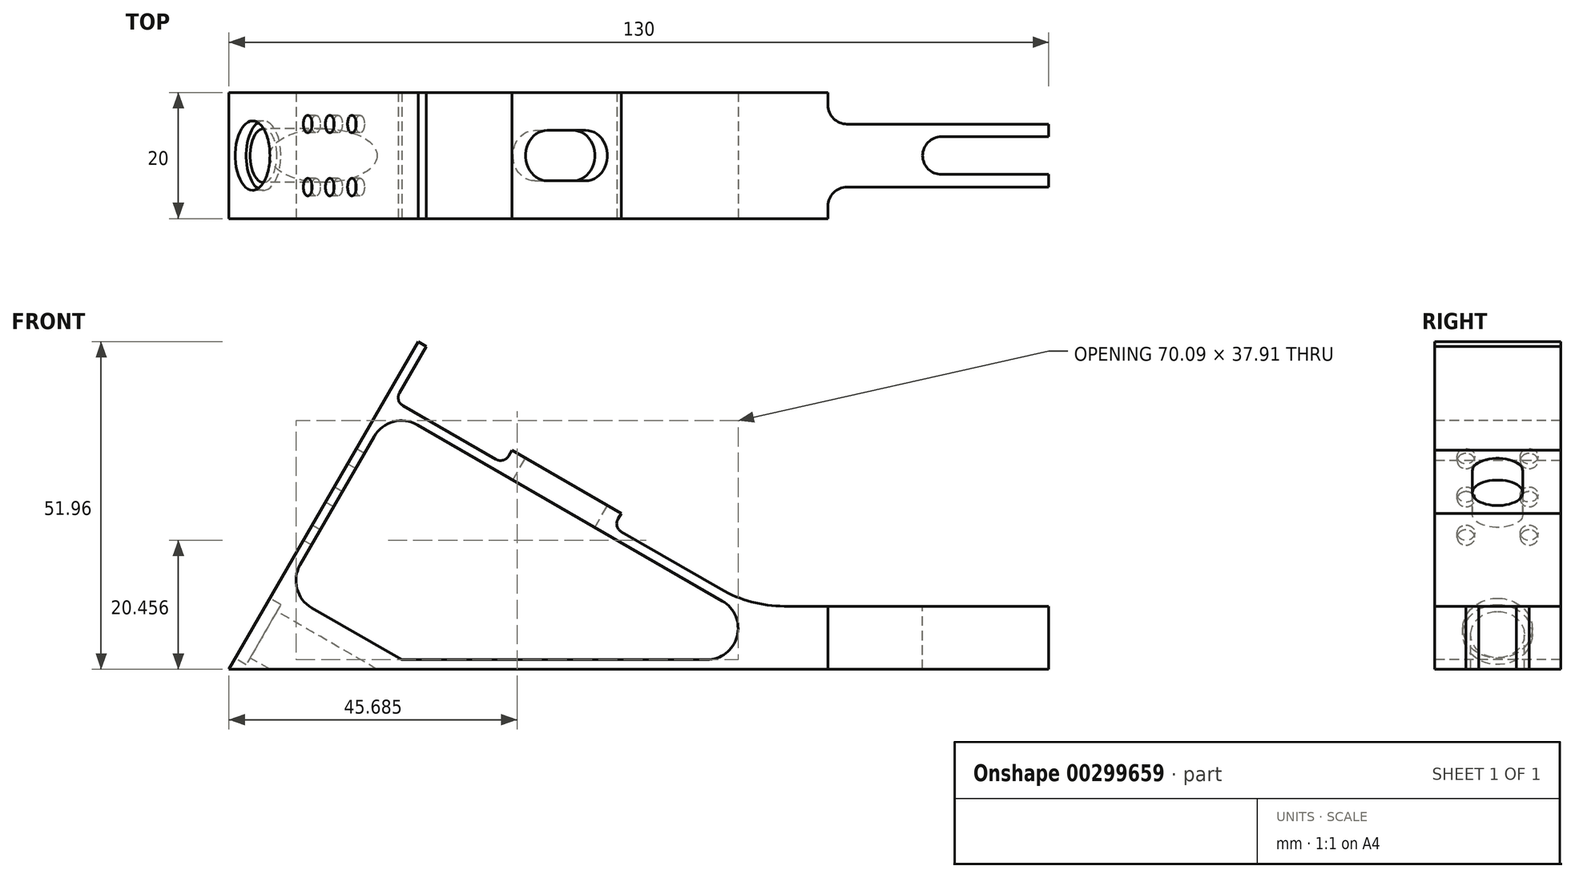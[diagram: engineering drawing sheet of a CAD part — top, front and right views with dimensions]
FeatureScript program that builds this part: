
annotation { "Feature Type Name" : "Feature", "Feature Type Description" : "" }
export const myFeature = defineFeature(function(context is Context, id is Id, definition is map)
    precondition{}
    {
        {
            var Q0;
            Q0=qCreatedBy(makeId("Front.planeOp"),FACE);
            var sketch = newSketch(context, id + "F0", { "sketchPlane" : qUnion([Q0])});
            skLineSegment(sketch, "E0", {"start": v(-65, 0) * mm, "end": v(65, 0) * mm});
            skLineSegment(sketch, "E1", {"start": v(65, 0) * mm, "end": v(65, 10) * mm});
            skLineSegment(sketch, "E2", {"start": v(65, 10) * mm, "end": v(23.04, 10) * mm});
            skArc(sketch, "E3", {"start": v(13.04, 12.68) * mm, "mid": v(17.86, 10.68) * mm, "end": v(23.04, 10) * mm});
            skLineSegment(sketch, "E4", {"start": v(-65, 0) * mm, "end": v(-35, 51.96) * mm});
            skLineSegment(sketch, "E5", {"start": v(-35, 51.96) * mm, "end": v(-33.7, 51.21) * mm});
            skLineSegment(sketch, "E6", {"start": v(-33.7, 51.21) * mm, "end": v(-37.95, 43.85) * mm});
            skLineSegment(sketch, "E7", {"start": v(-37.4, 41.8) * mm, "end": v(-22.68, 33.3) * mm});
            skLineSegment(sketch, "E8", {"start": v(-20.13, 34.72) * mm, "end": v(-2.8, 24.72) * mm});
            skLineSegment(sketch, "E9", {"start": v(13.04, 12.68) * mm, "end": v(-2.76, 21.8) * mm});
            skArc(sketch, "E10", {"start": v(-22.68, 33.3) * mm, "mid": v(-21.54, 33.15) * mm, "end": v(-20.63, 33.85) * mm});
            skLineSegment(sketch, "E11", {"start": v(-20.13, 34.72) * mm, "end": v(-20.63, 33.85) * mm});
            skLineSegment(sketch, "E12", {"start": v(-2.8, 24.72) * mm, "end": v(-3.3, 23.85) * mm});
            skArc(sketch, "E13", {"start": v(-3.3, 23.85) * mm, "mid": v(-3.46, 22.71) * mm, "end": v(-2.76, 21.8) * mm});
            skLineSegment(sketch, "E14", {"start": v(-53.7, 16.57) * mm, "end": v(-41.95, 36.92) * mm});
            skLineSegment(sketch, "E15", {"start": v(-35.12, 38.75) * mm, "end": v(13.24, 10.83) * mm});
            skLineSegment(sketch, "E16", {"start": v(-51.87, 9.74) * mm, "end": v(-37.6, 1.5) * mm});
            skLineSegment(sketch, "E17", {"start": v(-37.6, 1.5) * mm, "end": v(10.74, 1.5) * mm});
            skPoint(sketch, "E18.visualSharp", {"position": v(-56.2, 12.24) * mm});
            skArc(sketch, "E18.filletArc", {"start": v(-53.7, 16.57) * mm, "mid": v(-54.2, 12.78) * mm, "end": v(-51.87, 9.74) * mm});
            skPoint(sketch, "E19.visualSharp", {"position": v(-38.7, 42.55) * mm});
            skArc(sketch, "E19.filletArc", {"start": v(-37.95, 43.85) * mm, "mid": v(-38.1, 42.71) * mm, "end": v(-37.4, 41.8) * mm});
            skPoint(sketch, "E20.visualSharp", {"position": v(-39.45, 41.25) * mm});
            skArc(sketch, "E20.filletArc", {"start": v(-35.12, 38.75) * mm, "mid": v(-38.91, 39.25) * mm, "end": v(-41.95, 36.92) * mm});
            skPoint(sketch, "E21.visualSharp", {"position": v(29.4, 1.5) * mm});
            skArc(sketch, "E21.filletArc", {"start": v(10.74, 1.5) * mm, "mid": v(15.57, 5.2) * mm, "end": v(13.24, 10.83) * mm});
            skSolve(sketch);
        }
        {
            var Q0;
            Q0=makeQuery(id+"F0.imprint","IMPRINT",FACE,{"disambiguationData":[TD([[makeQuery(id+"F0.imprint","IMPRINT",EDGE,{"derivedFrom":sQuery(id+"F0.wireOp",EDGE,"E0")}),1.0]])]});
            extrude(context, id + "F1", {"entities" : qUnion([Q0]), "oppositeDirection" : true, "depth" : 20 * mm});
        }
        {
            var Q0;
            Q0=makeQuery(id+"F1.opExtrude","SWEPT_FACE",FACE,{"disambiguationData":[OSD([sQuery(id+"F0.wireOp",EDGE,"E8")])]});
            var sketch = newSketch(context, id + "F2", { "sketchPlane" : qUnion([Q0])});
            skLineSegment(sketch, "E22", {"start": v(-34.8, 10) * mm, "end": v(-14.8, 10) * mm, "construction": true});
            skLineSegment(sketch, "E23", {"start": v(-28.3, 6) * mm, "end": v(-21.3, 6) * mm});
            skArc(sketch, "E24", {"start": v(-21.3, 6) * mm, "mid": v(-17.3, 10) * mm, "end": v(-21.3, 14) * mm});
            skArc(sketch, "E25", {"start": v(-28.3, 14) * mm, "mid": v(-32.3, 10) * mm, "end": v(-28.3, 6) * mm});
            skLineSegment(sketch, "E26", {"start": v(-28.3, 14) * mm, "end": v(-21.3, 14) * mm});
            skLineSegment(sketch, "E27", {"start": v(-24.8, 0) * mm, "end": v(-24.8, 20) * mm, "construction": true});
            skLineSegment(sketch, "E28", {"start": v(-21.3, 0) * mm, "end": v(-21.3, 20) * mm, "construction": true});
            skLineSegment(sketch, "E29", {"start": v(-28.3, 0) * mm, "end": v(-28.3, 20) * mm, "construction": true});
            skSolve(sketch);
        }
        {
            var Q0;
            Q0 = qSketchRegion(id + "F2", true);
            var Q1;
            Q1=makeQuery(id+"F1.opExtrude","SWEPT_FACE",FACE,{"disambiguationData":[OSD([sQuery(id+"F0.wireOp",EDGE,"E15")])]});
            extrude(context, id + "F3", {"entities" : qUnion([Q0]), "operationType" : NewBodyOperationType.REMOVE, "endBound" : BoundingType.UP_TO_SURFACE, "oppositeDirection" : true, "endBoundEntityFace" : qUnion([Q1]), "depth" : 25 * mm});
        }
        {
            var Q0;
            Q0=makeQuery(id+"F1.opExtrude","SWEPT_FACE",FACE,{"disambiguationData":[OSD([sQuery(id+"F0.wireOp",EDGE,"E2")])]});
            var sketch = newSketch(context, id + "F4", { "sketchPlane" : qUnion([Q0])});
            skLineSegment(sketch, "E30", {"start": v(65, 7) * mm, "end": v(48, 7) * mm});
            skLineSegment(sketch, "E31", {"start": v(65, 13) * mm, "end": v(48, 13) * mm});
            skArc(sketch, "E32", {"start": v(48, 13) * mm, "mid": v(45, 10) * mm, "end": v(48, 7) * mm});
            skLineSegment(sketch, "E33", {"start": v(65, 13) * mm, "end": v(65, 7) * mm});
            skLineSegment(sketch, "E34", {"start": v(65, 5) * mm, "end": v(33, 5) * mm});
            skLineSegment(sketch, "E35", {"start": v(65, 15) * mm, "end": v(33, 15) * mm});
            skLineSegment(sketch, "E36", {"start": v(30, 20) * mm, "end": v(30, 18) * mm});
            skLineSegment(sketch, "E37", {"start": v(30, 0) * mm, "end": v(30, 2) * mm});
            skArc(sketch, "E38", {"start": v(33, 5) * mm, "mid": v(30.88, 4.12) * mm, "end": v(30, 2) * mm});
            skArc(sketch, "E39", {"start": v(30, 18) * mm, "mid": v(30.88, 15.88) * mm, "end": v(33, 15) * mm});
            skSolve(sketch);
        }
        {
            var Q0;
            Q0=makeQuery(id+"F4.imprint","IMPRINT",FACE,{"disambiguationData":[TD([[makeQuery(id+"F4.imprint","IMPRINT",EDGE,{"derivedFrom":sQuery(id+"F4.wireOp",EDGE,"E30")}),-1.0]])]});
            extrude(context, id + "F5", {"entities" : qUnion([Q0]), "operationType" : NewBodyOperationType.REMOVE, "endBound" : BoundingType.THROUGH_ALL, "oppositeDirection" : true, "depth" : 25 * mm});
        }
        {
            var Q0;
            Q0=makeQuery(id+"F1.opExtrude","SWEPT_FACE",FACE,{"disambiguationData":[OSD([sQuery(id+"F0.wireOp",EDGE,"E4")])]});
            var sketch = newSketch(context, id + "F6", { "sketchPlane" : qUnion([Q0])});
            skCircle(sketch, "E40", {"center": v(-10, -25) * mm, "radius": 4.25 * mm});
            skLineSegment(sketch, "E41", {"start": v(-15, -32.5) * mm, "end": v(-15, -7.5) * mm, "construction": true});
            skLineSegment(sketch, "E42", {"start": v(-20, -7.5) * mm, "end": v(-15, -7.5) * mm, "construction": true});
            skCircle(sketch, "E43", {"center": v(-15, -7.5) * mm, "radius": 1.4 * mm});
            skCircle(sketch, "E44.0.1.0", {"center": v(-15, -0.5) * mm, "radius": 1.4 * mm});
            skCircle(sketch, "E44.0.2.0", {"center": v(-15, 6.5) * mm, "radius": 1.4 * mm});
            skCircle(sketch, "E44.1.0.0", {"center": v(-5, -7.5) * mm, "radius": 1.4 * mm});
            skCircle(sketch, "E44.1.1.0", {"center": v(-5, -0.5) * mm, "radius": 1.4 * mm});
            skCircle(sketch, "E44.1.2.0", {"center": v(-5, 6.5) * mm, "radius": 1.4 * mm});
            skLineSegment(sketch, "E44.direction1", {"start": v(-15, -7.5) * mm, "end": v(-5, -7.5) * mm, "construction": true});
            skLineSegment(sketch, "E44.direction2", {"start": v(-15, -7.5) * mm, "end": v(-15, -0.5) * mm, "construction": true});
            skSolve(sketch);
        }
        {
            var Q0;
            Q0 = qSketchRegion(id + "F6", true);
            extrude(context, id + "F7", {"entities" : qUnion([Q0]), "operationType" : NewBodyOperationType.REMOVE, "endBound" : BoundingType.UP_TO_NEXT, "oppositeDirection" : true, "depth" : 25 * mm});
        }
        {
            var Q0;
            Q0=makeQuery(id+"F1.opExtrude","SWEPT_FACE",FACE,{"disambiguationData":[OSD([sQuery(id+"F0.wireOp",EDGE,"E4")])]});
            var sketch = newSketch(context, id + "F8", { "sketchPlane" : qUnion([Q0])});
            skCircle(sketch, "E45", {"center": v(-10, -25) * mm, "radius": 5.5 * mm});
            skSolve(sketch);
        }
        {
            var Q0;
            Q0 = qSketchRegion(id + "F8", true);
            extrude(context, id + "F9", {"entities" : qUnion([Q0]), "operationType" : NewBodyOperationType.REMOVE, "oppositeDirection" : true, "depth" : 2 * mm});
        }
        {
            var Q0;
            {var subQ4=sQuery(id+"F4.wireOp",EDGE,"E35");Q0=makeQuery(id+"F4.imprint","IMPRINT",FACE,{"disambiguationData":[TD([[makeQuery(id+"F4.imprint","IMPRINT",EDGE,{"derivedFrom":subQ4}),-1.0]])]});}
            var Q1;
            {var subQ4=sQuery(id+"F4.wireOp",EDGE,"E34");Q1=makeQuery(id+"F4.imprint","IMPRINT",FACE,{"disambiguationData":[TD([[makeQuery(id+"F4.imprint","IMPRINT",EDGE,{"derivedFrom":subQ4}),1.0]])]});}
            extrude(context, id + "F10", {"entities" : qUnion([Q0, Q1]), "operationType" : NewBodyOperationType.REMOVE, "endBound" : BoundingType.THROUGH_ALL, "oppositeDirection" : true, "depth" : 25 * mm});
        }
    });
